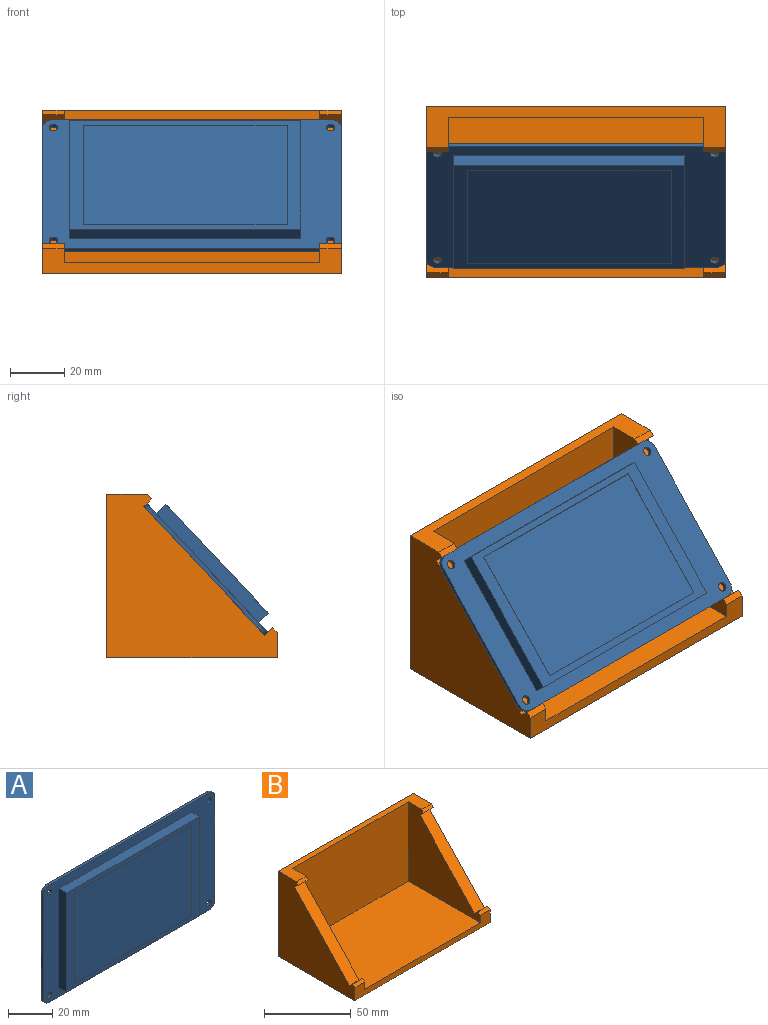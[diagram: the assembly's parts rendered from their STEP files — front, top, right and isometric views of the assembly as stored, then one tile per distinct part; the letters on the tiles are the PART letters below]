
ASSEMBLY  parts=2 mates=1
PART A: 24 faces, bbox 110x6.5x65 mm
  f0: plane 85x55mm, normal (0,-1,0), area 925mm2, adj f1,f2,f3,f4,f19,f20,f21,f22
  f1: plane 55x5mm, normal (1,0,0), area 275mm2, adj f0,f2,f4,f5
  f2: plane 85x5mm, normal (0,0,1), area 425mm2, adj f0,f1,f3,f5
  f3: plane 55x5mm, normal (-1,0,0), area 275mm2, adj f0,f2,f4,f5
  f4: plane 85x5mm, normal (0,0,-1), area 425mm2, adj f0,f1,f3,f5
  f5: plane 110x65mm, normal (0,-1,0), area 2429.1mm2, adj f1,f2,f3,f4,f6,f7,f8,f9
  f6: plane 102x1.5mm, normal (0,0,1), area 153mm2, adj f5,f10,f11,f14
  f7: plane 57x1.5mm, normal (1,0,0), area 85.5mm2, adj f5,f10,f11,f12
  f8: plane 102x1.5mm, normal (0,0,-1), area 153mm2, adj f5,f10,f12,f13
  f9: plane 57x1.5mm, normal (-1,0,0), area 85.5mm2, adj f5,f10,f13,f14
  f10: plane 110x65mm, normal (0,1,0), area 7104.1mm2, adj f6,f7,f8,f9,f11,f12,f13,f14
  f11: cylinder r=4mm len=4mm, axis (0,1,0), area 9.4mm2, adj f5,f6,f7,f10
  f12: cylinder r=4mm len=4mm, axis (0,-1,0), area 9.4mm2, adj f5,f7,f8,f10
  f13: cylinder r=4mm len=4mm, axis (0,1,0), area 9.4mm2, adj f5,f8,f9,f10
  f14: cylinder r=4mm len=4mm, axis (0,-1,0), area 9.4mm2, adj f5,f6,f9,f10
  f15: cylinder r=1.6mm len=3.2mm, axis (0,-1,0), area 15.1mm2, adj f5,f10
  f16: cylinder r=1.6mm len=3.2mm, axis (0,-1,0), area 15.1mm2, adj f5,f10
  f17: cylinder r=1.6mm len=3.2mm, axis (0,-1,0), area 15.1mm2, adj f5,f10
  f18: cylinder r=1.6mm len=3.2mm, axis (0,-1,0), area 15.1mm2, adj f5,f10
  f19: plane 50x0.1mm, normal (-1,0,0), area 5mm2, adj f0,f20,f22,f23
  f20: plane 75x0.1mm, normal (0,0,-1), area 7.5mm2, adj f0,f19,f21,f23
  f21: plane 50x0.1mm, normal (1,0,0), area 5mm2, adj f0,f20,f22,f23
  f22: plane 75x0.1mm, normal (0,0,1), area 7.5mm2, adj f0,f19,f21,f23
  f23: plane 75x50mm, normal (0,-1,0), area 3750mm2, adj f19,f20,f21,f22
PART B: 20 faces, bbox 110x62.7x60 mm
  f0: plane 94x56mm, normal (0,-1,0), area 5264mm2, adj f6,f11,f12,f19
  f1: plane 8x1.81mm, normal (0,-0.73,0.68), area 19.9mm2, adj f8,f10,f12,f15
  f2: plane 8x1.81mm, normal (0,-0.73,0.68), area 19.9mm2, adj f8,f9,f11,f16
  f3: plane 110x62.74mm, normal (0,0,-1), area 6901.4mm2, adj f5,f8,f9,f10
  f4: plane 8x1.64mm, normal (0,-0.73,0.68), area 18.1mm2, adj f6,f10,f12,f13
  f5: plane 110x60mm, normal (0,1,0), area 6600mm2, adj f3,f6,f9,f10
  f6: plane 110x14.99mm, normal (0,0,1), area 615.9mm2, adj f0,f4,f5,f7,f9,f10,f11,f12
  f7: plane 8x1.64mm, normal (0,-0.73,0.68), area 18.1mm2, adj f6,f9,f11,f18
  f8: plane 110x9.17mm, normal (0,-1,0), area 522.7mm2, adj f1,f2,f3,f9,f10,f11,f12,f19
  f9: plane 62.74x60mm, normal (1,0,0), area 2291mm2, adj f2,f3,f5,f6,f7,f8,f16,f17
  f10: plane 62.74x60mm, normal (-1,0,0), area 2291mm2, adj f1,f3,f4,f5,f6,f8,f13,f14
  f11: plane 58.74x56mm, normal (-1,0,0), area 1816mm2, adj f0,f2,f6,f7,f8,f16,f17,f18
  f12: plane 58.74x56mm, normal (1,0,0), area 1816mm2, adj f0,f1,f4,f6,f8,f13,f14,f15
  f13: plane 8x2.92mm, normal (0,-0.68,-0.73), area 32mm2, adj f4,f10,f12,f14
  f14: plane 47.38x44.5mm, normal (0,-0.73,0.68), area 520mm2, adj f10,f12,f13,f15
  f15: plane 8x2.92mm, normal (0,0.68,0.73), area 32mm2, adj f1,f10,f12,f14
  f16: plane 8x2.92mm, normal (0,0.68,0.73), area 32mm2, adj f2,f9,f11,f17
  f17: plane 47.38x44.5mm, normal (0,-0.73,0.68), area 520mm2, adj f9,f11,f16,f18
  f18: plane 8x2.92mm, normal (0,-0.68,-0.73), area 32mm2, adj f7,f9,f11,f17
  f19: plane 94x58.74mm, normal (0,0,1), area 5521.6mm2, adj f0,f8,f11,f12
PLACE A rot(axis=(-1,0,0),43.2deg) t=(-2.5,-36.97,2.96)mm
PLACE B t=(0,0,-30)mm
MATE fastened B.f14 <-> A.f10  axis (0,-0.73,0.68) through (-55,-35.87,1.93)mm
